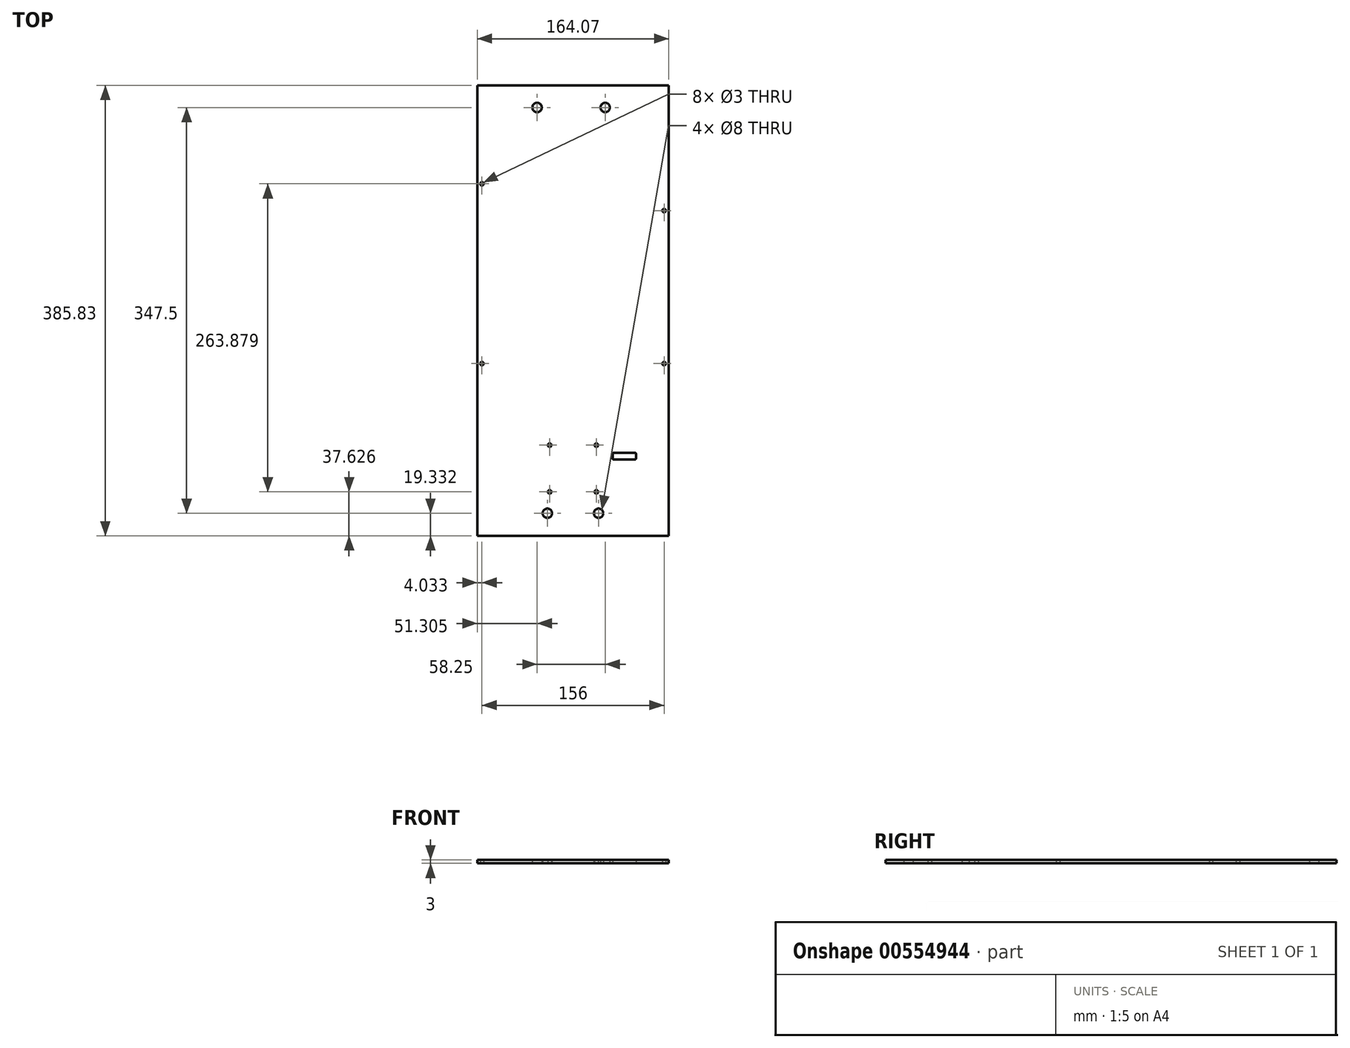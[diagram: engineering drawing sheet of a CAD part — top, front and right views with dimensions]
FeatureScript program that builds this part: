
annotation { "Feature Type Name" : "Feature", "Feature Type Description" : "" }
export const myFeature = defineFeature(function(context is Context, id is Id, definition is map)
    precondition{}
    {
        {
            var Q0;
            Q0=qCreatedBy(makeId("Top.planeOp"),FACE);
            var sketch = newSketch(context, id + "F0", { "sketchPlane" : qUnion([Q0])});
            skPoint(sketch, "E0.middle", {"position": v(0, 0) * mm});
            skLineSegment(sketch, "E1.bottom", {"start": v(-65.5, 95.27) * mm, "end": v(65.5, 95.27) * mm, "construction": true});
            skLineSegment(sketch, "E1.top", {"start": v(-65.5, -53.23) * mm, "end": v(65.5, -53.23) * mm, "construction": true});
            skLineSegment(sketch, "E1.left", {"start": v(-65.5, 95.27) * mm, "end": v(-65.5, -53.23) * mm, "construction": true});
            skLineSegment(sketch, "E1.right", {"start": v(65.5, 95.27) * mm, "end": v(65.5, -53.23) * mm, "construction": true});
            skPoint(sketch, "E2", {"position": v(0, 95.27) * mm});
            skPoint(sketch, "E3", {"position": v(-40, 95.27) * mm});
            skPoint(sketch, "E4", {"position": v(-40, -53.23) * mm});
            skPoint(sketch, "E5", {"position": v(-33, 95.27) * mm});
            skLineSegment(sketch, "E6", {"start": v(-40, 95.27) * mm, "end": v(-40, 90.27) * mm, "construction": true});
            skLineSegment(sketch, "E7", {"start": v(-33, 95.27) * mm, "end": v(-33, 90.27) * mm, "construction": true});
            skLineSegment(sketch, "E8", {"start": v(-40, 90.27) * mm, "end": v(-33, 90.27) * mm, "construction": true});
            skLineSegment(sketch, "E9.MirrorCS", {"start": v(-40, -48.23) * mm, "end": v(-33, -48.23) * mm, "construction": true});
            skLineSegment(sketch, "E10.MirrorCS", {"start": v(-40, -53.23) * mm, "end": v(-40, -48.23) * mm, "construction": true});
            skLineSegment(sketch, "E11.MirrorCS", {"start": v(-33, -53.23) * mm, "end": v(-33, -48.23) * mm, "construction": true});
            skPoint(sketch, "E12.MirrorP", {"position": v(-33, -53.23) * mm});
            skPoint(sketch, "E13.MirrorP", {"position": v(40, 95.27) * mm});
            skLineSegment(sketch, "E14.MirrorCS", {"start": v(40, 95.27) * mm, "end": v(40, 90.27) * mm, "construction": true});
            skLineSegment(sketch, "E15.MirrorCS", {"start": v(40, 90.27) * mm, "end": v(33, 90.27) * mm, "construction": true});
            skLineSegment(sketch, "E16.MirrorCS", {"start": v(33, 95.27) * mm, "end": v(33, 90.27) * mm, "construction": true});
            skPoint(sketch, "E17.MirrorP", {"position": v(33, 95.27) * mm});
            skPoint(sketch, "E18.MirrorP", {"position": v(40, -53.23) * mm});
            skLineSegment(sketch, "E19.MirrorCS", {"start": v(40, -48.23) * mm, "end": v(33, -48.23) * mm, "construction": true});
            skPoint(sketch, "E20.MirrorP", {"position": v(33, -53.23) * mm});
            skLineSegment(sketch, "E21.MirrorCS", {"start": v(33, -53.23) * mm, "end": v(33, -48.23) * mm, "construction": true});
            skLineSegment(sketch, "E22.MirrorCS", {"start": v(40, -53.23) * mm, "end": v(40, -48.23) * mm, "construction": true});
            skPoint(sketch, "E23", {"position": v(55.5, -173.31) * mm});
            skLineSegment(sketch, "E24.bottom", {"start": v(54.5, -173.31) * mm, "end": v(36.5, -173.31) * mm});
            skLineSegment(sketch, "E24.top", {"start": v(54.5, -179.31) * mm, "end": v(36.5, -179.31) * mm});
            skLineSegment(sketch, "E24.left", {"start": v(55.5, -174.31) * mm, "end": v(55.5, -178.31) * mm});
            skLineSegment(sketch, "E24.right", {"start": v(35.5, -174.31) * mm, "end": v(35.5, -178.31) * mm});
            skPoint(sketch, "E25.visualSharp", {"position": v(35.5, -179.31) * mm});
            skArc(sketch, "E25.filletArc", {"start": v(35.5, -178.31) * mm, "mid": v(35.8, -179.02) * mm, "end": v(36.5, -179.31) * mm});
            skPoint(sketch, "E26.visualSharp", {"position": v(55.5, -179.31) * mm});
            skArc(sketch, "E26.filletArc", {"start": v(54.5, -179.31) * mm, "mid": v(55.2, -179.02) * mm, "end": v(55.5, -178.31) * mm});
            skArc(sketch, "E27.filletArc", {"start": v(55.5, -174.31) * mm, "mid": v(55.2, -173.6) * mm, "end": v(54.5, -173.31) * mm});
            skPoint(sketch, "E28.visualSharp", {"position": v(35.5, -173.31) * mm});
            skArc(sketch, "E28.filletArc", {"start": v(36.5, -173.31) * mm, "mid": v(35.8, -173.6) * mm, "end": v(35.5, -174.31) * mm});
            skPoint(sketch, "E29", {"position": v(1.6, 138.27) * mm});
            skCircle(sketch, "E30.MirrorC", {"center": v(-29.13, 122.27) * mm, "radius": 4 * mm});
            skCircle(sketch, "E31.MirrorC", {"center": v(29.12, 122.27) * mm, "radius": 4 * mm});
            skCircle(sketch, "E32.MirrorC", {"center": v(-20.32, -225.23) * mm, "radius": 4 * mm});
            skCircle(sketch, "E33.MirrorC", {"center": v(23.53, -225.23) * mm, "radius": 4 * mm});
            skPoint(sketch, "E34.center.orphan", {"position": v(-19.35, 122.27) * mm});
            skPoint(sketch, "E35.MirrorC.center.orphan", {"position": v(22.56, 122.27) * mm});
            skPoint(sketch, "E36.trimOffspring.end.orphan", {"position": v(75, 3.52) * mm});
            skPoint(sketch, "E37.start.orphan", {"position": v(-71.8, 3.52) * mm});
            skPoint(sketch, "E38.middle", {"position": v(1.6, -186.93) * mm});
            skCircle(sketch, "E39", {"center": v(21.6, -206.93) * mm, "radius": 1.5 * mm});
            skCircle(sketch, "E40", {"center": v(-18.4, -206.93) * mm, "radius": 1.5 * mm});
            skCircle(sketch, "E41", {"center": v(-18.4, -166.93) * mm, "radius": 1.5 * mm});
            skCircle(sketch, "E42", {"center": v(21.6, -166.93) * mm, "radius": 1.5 * mm});
            skCircle(sketch, "E43", {"center": v(-20.32, -225.23) * mm, "radius": 10 * mm, "construction": true});
            skCircle(sketch, "E44", {"center": v(23.53, -225.23) * mm, "radius": 10 * mm, "construction": true});
            skLineSegment(sketch, "E45", {"start": v(75, 138.27) * mm, "end": v(75, -241.56) * mm, "construction": true});
            skLineSegment(sketch, "E46", {"start": v(-71.8, -241.56) * mm, "end": v(75, -241.56) * mm, "construction": true});
            skLineSegment(sketch, "E47", {"start": v(-71.8, -241.56) * mm, "end": v(-71.8, 138.27) * mm, "construction": true});
            skLineSegment(sketch, "E48", {"start": v(-71.8, 138.27) * mm, "end": v(75, 138.27) * mm, "construction": true});
            skPoint(sketch, "E49", {"position": v(-76.4, -97.05) * mm});
            skPoint(sketch, "E50", {"position": v(79.6, -97.05) * mm});
            skPoint(sketch, "E51", {"position": v(79.6, 33.95) * mm});
            skPoint(sketch, "E52", {"position": v(-76.4, 56.95) * mm});
            skCircle(sketch, "E53", {"center": v(-76.4, 56.95) * mm, "radius": 1.5 * mm});
            skCircle(sketch, "E54", {"center": v(79.6, 33.95) * mm, "radius": 1.5 * mm});
            skCircle(sketch, "E55", {"center": v(79.6, -97.05) * mm, "radius": 1.5 * mm});
            skCircle(sketch, "E56", {"center": v(-76.4, -97.05) * mm, "radius": 1.5 * mm});
            skLineSegment(sketch, "E57", {"start": v(1.6, -241.56) * mm, "end": v(1.6, 138.27) * mm});
            skPoint(sketch, "E58", {"position": v(1.6, -51.64) * mm});
            skLineSegment(sketch, "E59.bottom", {"start": v(83.64, -244.56) * mm, "end": v(-80.43, -244.56) * mm});
            skLineSegment(sketch, "E59.top", {"start": v(83.64, 141.27) * mm, "end": v(-80.43, 141.27) * mm});
            skLineSegment(sketch, "E59.left", {"start": v(83.64, -244.56) * mm, "end": v(83.64, 141.27) * mm});
            skLineSegment(sketch, "E59.right", {"start": v(-80.43, -244.56) * mm, "end": v(-80.43, 141.27) * mm});
            skSolve(sketch);
        }
        {
            var Q0;
            Q0 = qSketchRegion(id + "F0", true);
            extrude(context, id + "F1", {"entities" : qUnion([Q0]), "depth" : 3 * mm, "offsetDistance" : 25 * mm});
        }
    });
